# Revit family: BE_77069_de_DE
name_source: partatom
category: Lighting Fixtures
revit_build: Autodesk Revit 2015 (Build: 20160512_0715(x64)
units: mm (PartAtom-declared; Revit-internal decimal feet)

## types (2) — shared parameters
AC/DC = DC
Aktualisierung = 2016-12-14T04:15:04
Anschlussleitung = 1.8 m 05RN8-F 2 × 1²
Apparent Load = 0 VA
BEGA_Dummy = No
BEGA_IES = Yes
BEGA_Intern = Yes
BEGA_Intern_Konstruktion = Yes
BEGA_Intern_an = Yes
BEGA_Intern_aus = Yes
Befestigungsbohrung = Ø 6,5 mm
Belastbarkeit = 1000 kg
Beschreibung_Sonderanfertigung = Hier können Sie Informationen zur Sonderanfertigung eintragen.
Bestellnummer_Erdstück = ---
CE_Konformität = ja
Color Filter = 16777215
Description = Bodenaufbauleuchte
Dimming Lamp Color Temperature Shift = <None>
ENEC = ja
Einbaugehäuse = No
Energieeffizienzklasse = LED A++ - A
Erdstück = No
Farbwiedergabeindex = Ra > 80
Gewicht = 0.95 kg
Lamp = LED 1.2 W
Lastklassifizierung = Beleuchtung
Lebensdauerkriterien = L70 = 50.000 h
Logo = BEGA_Logo.png
M_A = No
M_G = Yes
M_W = No
Manufacturer = BEGA
Material_02 = BEGA_Oberfläche_Silber_matt
Material_03 = BEGA_Oberfläche_Weiss_matt
Material_06 = BEGA_Oberfläche_Edelstahl_gebürstet
Material_09 = BEGA_Glas_klar
Material_11 = BEGA_Glas_opal
Material_15 = BEGA_Leuchtmedium_matt
Material_17 = BEGA_Reflektor
Oberflächentemperatur = 20 °C
Produktdatenblatt = http://www.bega.de
Schutzart = IP 67
Schutzklasse = III
Sonderanfertigung = No
Spannung = 24 V
Tilt Angle = 0.00°
Type Image = 77069.png
URL = http://www.bega.de
Umgebungstemperatur = 25 °C
zero-valued in all types: Default Elevation

## per-type parameters (varying)
| type | Bestellnummer | Farbtemperatur | LED_Modulbezeichnung | Lampenlichtstrom | Leuchtenlichtstrom | Model | Photometric Web File |
| BEGA_77069_Grafit_K4 | 77069K4 | 4000 K | LED-0287/840 | 114 lm | 17 lm | 77069K4 | BE_77069K4.IES |
| BEGA_77069_Grafit_K3 | 77069 | 3000 K | LED-0287/830 | 105 lm | 16 lm | 77069 | BE_77069.IES |
